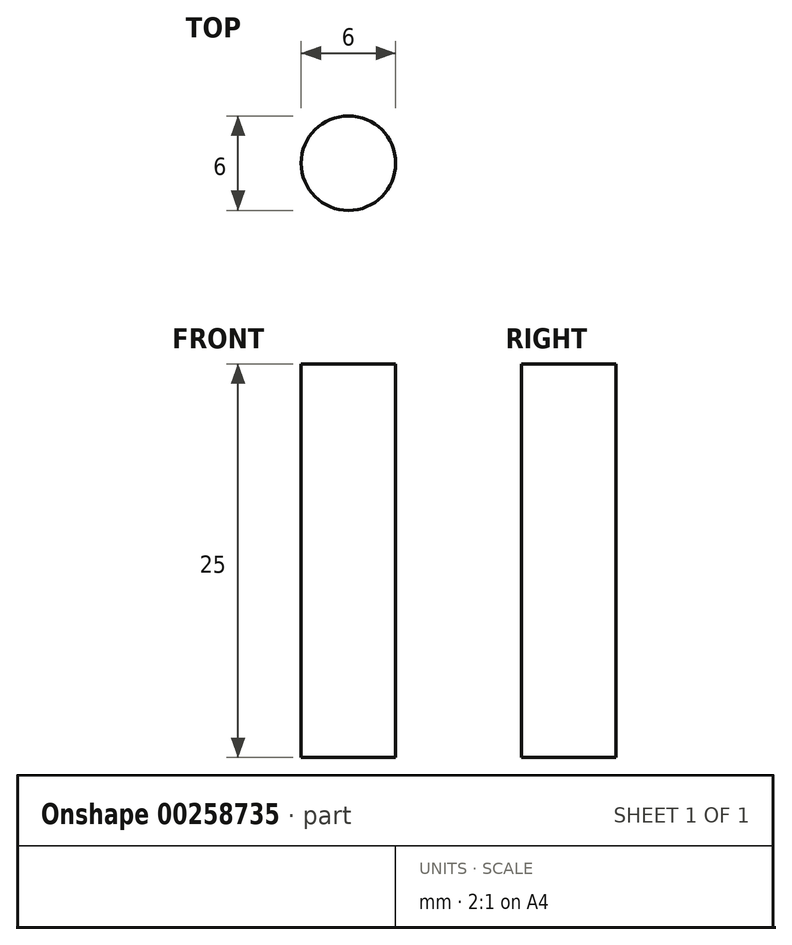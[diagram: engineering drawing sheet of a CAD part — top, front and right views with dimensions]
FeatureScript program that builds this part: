
annotation { "Feature Type Name" : "Feature", "Feature Type Description" : "" }
export const myFeature = defineFeature(function(context is Context, id is Id, definition is map)
    precondition{}
    {
        {
            var Q0;
            Q0=qCreatedBy(makeId("Top.planeOp"),FACE);
            var sketch = newSketch(context, id + "F1", { "sketchPlane" : qUnion([Q0])});
            skLineSegment(sketch, "E0.bottom", {"start": v(0, 0) * mm, "end": v(1050, 0) * mm});
            skLineSegment(sketch, "E0.top", {"start": v(0, 400) * mm, "end": v(1050, 400) * mm});
            skLineSegment(sketch, "E0.left", {"start": v(0, 0) * mm, "end": v(0, 400) * mm});
            skLineSegment(sketch, "E0.right", {"start": v(1090, 40) * mm, "end": v(1090, 360) * mm});
            skLineSegment(sketch, "E1.top", {"start": v(1090, 360) * mm, "end": v(1050, 360) * mm});
            skLineSegment(sketch, "E1.right", {"start": v(1050, 400) * mm, "end": v(1050, 360) * mm});
            skLineSegment(sketch, "E2", {"start": v(1050, 0) * mm, "end": v(1050, 40) * mm});
            skLineSegment(sketch, "E3", {"start": v(1050, 40) * mm, "end": v(1090, 40) * mm});
            skSolve(sketch);
        }
        {
            var Q0;
            Q0=makeQuery(id+"F1.imprint","IMPRINT",FACE,{"disambiguationData":[TD([[makeQuery(id+"F1.imprint","IMPRINT",EDGE,{"derivedFrom":sQuery(id+"F1.wireOp",EDGE,"E0.bottom")}),1.0]])]});
            extrude(context, id + "F2", {"entities" : qUnion([Q0]), "depth" : 25 * mm});
        }
        {
            var Q0;
            Q0=makeQuery(id+"F2.opExtrude","CAP_FACE",FACE,{"disambiguationData":[OSD([sQuery(id+"F1.wireOp",EDGE,"E0.bottom"),sQuery(id+"F1.wireOp",EDGE,"E0.top"),sQuery(id+"F1.wireOp",EDGE,"E0.left"),sQuery(id+"F1.wireOp",EDGE,"E0.right"),sQuery(id+"F1.wireOp",EDGE,"E1.top"),sQuery(id+"F1.wireOp",EDGE,"E1.right"),sQuery(id+"F1.wireOp",EDGE,"E2"),sQuery(id+"F1.wireOp",EDGE,"E3")])],"isStart":false});
            var sketch = newSketch(context, id + "F0", { "sketchPlane" : qUnion([Q0])});
            skCircle(sketch, "E4", {"center": v(1030, 120) * mm, "radius": 3 * mm});
            skLineSegment(sketch, "E5", {"start": v(1090, 200) * mm, "end": v(901.88, 200) * mm, "construction": true});
            skCircle(sketch, "E6.MirrorC", {"center": v(1030, 280) * mm, "radius": 3 * mm});
            skSolve(sketch);
        }
        {
            var Q0;
            Q0=makeQuery(id+"F0.imprint","IMPRINT",FACE,{"disambiguationData":[TD([[makeQuery(id+"F0.imprint","IMPRINT",EDGE,{"derivedFrom":sQuery(id+"F0.wireOp",EDGE,"E4")}),1.0]])]});
            var Q1;
            Q1=makeQuery(id+"F0.imprint","IMPRINT",FACE,{"disambiguationData":[TD([[makeQuery(id+"F0.imprint","IMPRINT",EDGE,{"derivedFrom":sQuery(id+"F0.wireOp",EDGE,"E6.MirrorC")}),-1.0]])]});
            extrude(context, id + "F3", {"entities" : qUnion([Q0, Q1]), "operationType" : NewBodyOperationType.REMOVE, "endBound" : BoundingType.THROUGH_ALL, "oppositeDirection" : true, "depth" : 10 * mm});
        }
    });
